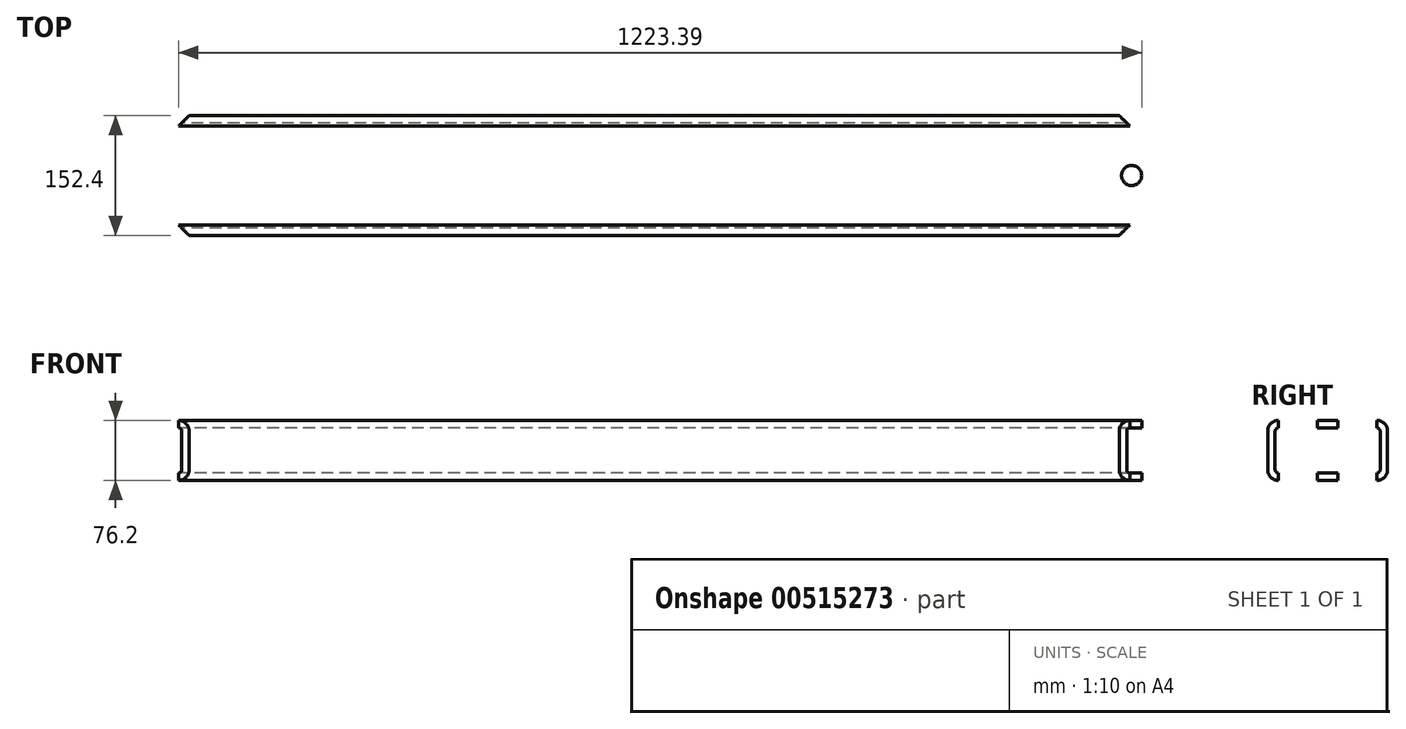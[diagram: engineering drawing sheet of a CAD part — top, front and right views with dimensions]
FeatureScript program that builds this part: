
annotation { "Feature Type Name" : "Feature", "Feature Type Description" : "" }
export const myFeature = defineFeature(function(context is Context, id is Id, definition is map)
    precondition{}
    {
        {
            var Q0;
            Q0=qCreatedBy(makeId("Right.planeOp"),FACE);
            var sketch = newSketch(context, id + "F0", { "sketchPlane" : qUnion([Q0])});
            skLineSegment(sketch, "E0.bottom", {"start": v(-62.67, 38.1) * mm, "end": v(62.67, 38.1) * mm});
            skLineSegment(sketch, "E0.top", {"start": v(-62.67, -38.1) * mm, "end": v(62.67, -38.1) * mm});
            skLineSegment(sketch, "E0.left", {"start": v(-76.2, 24.57) * mm, "end": v(-76.2, -24.57) * mm});
            skLineSegment(sketch, "E0.right", {"start": v(76.2, 24.57) * mm, "end": v(76.2, -24.57) * mm});
            skPoint(sketch, "E1.visualSharp", {"position": v(76.2, 38.1) * mm});
            skArc(sketch, "E1.filletArc", {"start": v(76.2, 24.57) * mm, "mid": v(72.24, 34.14) * mm, "end": v(62.67, 38.1) * mm});
            skPoint(sketch, "E2.visualSharp", {"position": v(-76.2, 38.1) * mm});
            skArc(sketch, "E2.filletArc", {"start": v(-62.67, 38.1) * mm, "mid": v(-72.24, 34.14) * mm, "end": v(-76.2, 24.57) * mm});
            skPoint(sketch, "E3.visualSharp", {"position": v(-76.2, -38.1) * mm});
            skArc(sketch, "E3.filletArc", {"start": v(-76.2, -24.57) * mm, "mid": v(-72.24, -34.14) * mm, "end": v(-62.67, -38.1) * mm});
            skPoint(sketch, "E4.visualSharp", {"position": v(76.2, -38.1) * mm});
            skArc(sketch, "E4.filletArc", {"start": v(62.67, -38.1) * mm, "mid": v(72.24, -34.14) * mm, "end": v(76.2, -24.57) * mm});
            skLineSegment(sketch, "E5.bottom", {"start": v(-62.67, -28.58) * mm, "end": v(62.67, -28.58) * mm});
            skLineSegment(sketch, "E5.top", {"start": v(-62.67, 28.58) * mm, "end": v(62.67, 28.58) * mm});
            skLineSegment(sketch, "E5.left", {"start": v(-66.67, -24.57) * mm, "end": v(-66.67, 24.57) * mm});
            skLineSegment(sketch, "E5.right", {"start": v(66.67, -24.57) * mm, "end": v(66.67, 24.57) * mm});
            skPoint(sketch, "E5.middle", {"position": v(0, 0) * mm});
            skPoint(sketch, "E6.visualSharp", {"position": v(66.67, 28.58) * mm});
            skArc(sketch, "E6.filletArc", {"start": v(66.68, 24.57) * mm, "mid": v(65.5, 27.4) * mm, "end": v(62.67, 28.58) * mm});
            skPoint(sketch, "E7.visualSharp", {"position": v(-66.67, 28.58) * mm});
            skArc(sketch, "E7.filletArc", {"start": v(-62.67, 28.58) * mm, "mid": v(-65.5, 27.4) * mm, "end": v(-66.67, 24.57) * mm});
            skPoint(sketch, "E8.visualSharp", {"position": v(-66.67, -28.58) * mm});
            skArc(sketch, "E8.filletArc", {"start": v(-66.67, -24.57) * mm, "mid": v(-65.5, -27.4) * mm, "end": v(-62.67, -28.58) * mm});
            skPoint(sketch, "E9.visualSharp", {"position": v(66.67, -28.58) * mm});
            skArc(sketch, "E9.filletArc", {"start": v(62.67, -28.58) * mm, "mid": v(65.5, -27.4) * mm, "end": v(66.68, -24.57) * mm});
            skSolve(sketch);
        }
        {
            var Q0;
            Q0=qSketchRegion(id+"F0",true);
            extrude(context, id + "F1", {"entities" : qUnion([Q0]), "endBound" : BoundingType.SYMMETRIC, "depth" : 1289.05 * mm, "offsetDistance" : 25.4 * mm});
        }
        {
            var Q0;
            Q0=makeQuery(id+"F1.opExtrude","SWEPT_FACE",FACE,{"disambiguationData":[OSD([sQuery(id+"F0.wireOp",EDGE,"E0.bottom")])]});
            var sketch = newSketch(context, id + "F2", { "sketchPlane" : qUnion([Q0])});
            skLineSegment(sketch, "E10", {"start": v(-644.52, 22.35) * mm, "end": v(-590.68, 76.2) * mm});
            skLineSegment(sketch, "E11", {"start": v(-590.68, 76.2) * mm, "end": v(-644.52, 76.2) * mm});
            skLineSegment(sketch, "E12", {"start": v(-644.52, 76.2) * mm, "end": v(-644.52, 22.35) * mm});
            skCircle(sketch, "E13", {"center": v(-606.42, 0) * mm, "radius": 12.76 * mm});
            skLineSegment(sketch, "E14.MirrorCS", {"start": v(-644.53, -22.35) * mm, "end": v(-590.68, -76.2) * mm});
            skLineSegment(sketch, "E15.MirrorCS", {"start": v(644.53, 22.35) * mm, "end": v(590.68, 76.2) * mm});
            skCircle(sketch, "E16.MirrorC", {"center": v(606.42, 0) * mm, "radius": 12.76 * mm});
            skLineSegment(sketch, "E17.MirrorCS", {"start": v(644.53, -22.35) * mm, "end": v(590.68, -76.2) * mm});
            skLineSegment(sketch, "E18.MirrorCS", {"start": v(644.52, 76.2) * mm, "end": v(644.52, 22.35) * mm});
            skLineSegment(sketch, "E19.MirrorCS", {"start": v(590.68, 76.2) * mm, "end": v(644.52, 76.2) * mm});
            skLineSegment(sketch, "E20.MirrorCS", {"start": v(-644.52, -76.2) * mm, "end": v(-644.52, -22.35) * mm});
            skLineSegment(sketch, "E21.MirrorCS", {"start": v(-590.68, -76.2) * mm, "end": v(-644.52, -76.2) * mm});
            skLineSegment(sketch, "E22.MirrorCS", {"start": v(590.68, -76.2) * mm, "end": v(644.52, -76.2) * mm});
            skLineSegment(sketch, "E23.MirrorCS", {"start": v(644.52, -76.2) * mm, "end": v(644.52, -22.35) * mm});
            skSolve(sketch);
        }
        {
            var Q0;
            Q0=makeQuery(id+"F2.imprint","IMPRINT",FACE,{"disambiguationData":[TD([[makeQuery(id+"F2.imprint","IMPRINT",EDGE,{"derivedFrom":sQuery(id+"F2.wireOp",EDGE,"E13")}),1.0]])]});
            var Q1;
            Q1=makeQuery(id+"F2.imprint","IMPRINT",FACE,{"disambiguationData":[TD([[makeQuery(id+"F2.imprint","IMPRINT",EDGE,{"derivedFrom":sQuery(id+"F2.wireOp",EDGE,"E16.MirrorC")}),-1.0]])]});
            var Q2;
            {var subQ0=sQuery(id+"F2.wireOp",EDGE,"E11");Q2=makeQuery(id+"F2.imprint","IMPRINT",FACE,{"disambiguationData":[TD([[makeQuery(id+"F2.imprint","IMPRINT",EDGE,{"derivedFrom":subQ0}),1.0]])]});}
            var Q3;
            {var subQ0=sQuery(id+"F2.wireOp",EDGE,"E21.MirrorCS");Q3=makeQuery(id+"F2.imprint","IMPRINT",FACE,{"disambiguationData":[TD([[makeQuery(id+"F2.imprint","IMPRINT",EDGE,{"derivedFrom":subQ0}),-1.0]])]});}
            var Q4;
            {var subQ0=sQuery(id+"F2.wireOp",EDGE,"E19.MirrorCS");Q4=makeQuery(id+"F2.imprint","IMPRINT",FACE,{"disambiguationData":[TD([[makeQuery(id+"F2.imprint","IMPRINT",EDGE,{"derivedFrom":subQ0}),-1.0]])]});}
            var Q5;
            {var subQ0=sQuery(id+"F2.wireOp",EDGE,"E22.MirrorCS");Q5=makeQuery(id+"F2.imprint","IMPRINT",FACE,{"disambiguationData":[TD([[makeQuery(id+"F2.imprint","IMPRINT",EDGE,{"derivedFrom":subQ0}),1.0]])]});}
            var Q6;
            {var subQ0=sQuery(id+"F2.wireOp",EDGE,"E18.MirrorCS");var subQ1=sQuery(id+"F2.wireOp",EDGE,"E15.MirrorCS");var subQ2=sQuery(id+"F0.wireOp",EDGE,"E0.bottom");var subQ3=makeQuery(id+"F2.imprint","INTERSECT",VERTEX,{"derivedFrom":[makeQuery(id+"F1.opExtrude","CAP_EDGE",EDGE,{"disambiguationData":[OSD([subQ2])],"isStart":false}),subQ1,subQ0]});Q6=makeQuery(id+"F2.imprint","IMPRINT",FACE,{"disambiguationData":[TD([[makeQuery(id+"F2.imprint","IMPRINT",EDGE,{"disambiguationData":[TD([[subQ3,-1.0]])],"derivedFrom":subQ1}),-1.0]])]});}
            var Q7;
            {var subQ0=sQuery(id+"F2.wireOp",EDGE,"E23.MirrorCS");var subQ1=sQuery(id+"F2.wireOp",EDGE,"E17.MirrorCS");var subQ2=sQuery(id+"F0.wireOp",EDGE,"E0.bottom");var subQ3=makeQuery(id+"F2.imprint","INTERSECT",VERTEX,{"derivedFrom":[makeQuery(id+"F1.opExtrude","CAP_EDGE",EDGE,{"disambiguationData":[OSD([subQ2])],"isStart":false}),subQ1,subQ0]});Q7=makeQuery(id+"F2.imprint","IMPRINT",FACE,{"disambiguationData":[TD([[makeQuery(id+"F2.imprint","IMPRINT",EDGE,{"disambiguationData":[TD([[subQ3,-1.0]])],"derivedFrom":subQ1}),1.0]])]});}
            var Q8;
            {var subQ0=sQuery(id+"F2.wireOp",EDGE,"E20.MirrorCS");var subQ1=sQuery(id+"F2.wireOp",EDGE,"E14.MirrorCS");var subQ2=sQuery(id+"F0.wireOp",EDGE,"E0.bottom");var subQ3=makeQuery(id+"F2.imprint","INTERSECT",VERTEX,{"derivedFrom":[makeQuery(id+"F1.opExtrude","CAP_EDGE",EDGE,{"disambiguationData":[OSD([subQ2])],"isStart":true}),subQ1,subQ0]});Q8=makeQuery(id+"F2.imprint","IMPRINT",FACE,{"disambiguationData":[TD([[makeQuery(id+"F2.imprint","IMPRINT",EDGE,{"disambiguationData":[TD([[subQ3,-1.0]])],"derivedFrom":subQ1}),-1.0]])]});}
            var Q9;
            {var subQ0=sQuery(id+"F2.wireOp",EDGE,"E12");var subQ1=sQuery(id+"F2.wireOp",EDGE,"E10");var subQ2=sQuery(id+"F0.wireOp",EDGE,"E0.bottom");var subQ3=makeQuery(id+"F2.imprint","INTERSECT",VERTEX,{"derivedFrom":[makeQuery(id+"F1.opExtrude","CAP_EDGE",EDGE,{"disambiguationData":[OSD([subQ2])],"isStart":true}),subQ1,subQ0]});Q9=makeQuery(id+"F2.imprint","IMPRINT",FACE,{"disambiguationData":[TD([[makeQuery(id+"F2.imprint","IMPRINT",EDGE,{"disambiguationData":[TD([[subQ3,-1.0]])],"derivedFrom":subQ1}),1.0]])]});}
            extrude(context, id + "F3", {"entities" : qUnion([Q0, Q1, Q2, Q3, Q4, Q5, Q6, Q7, Q8, Q9]), "operationType" : NewBodyOperationType.REMOVE, "endBound" : BoundingType.THROUGH_ALL, "oppositeDirection" : true, "depth" : 25.4 * mm, "offsetDistance" : 25.4 * mm});
        }
    });
